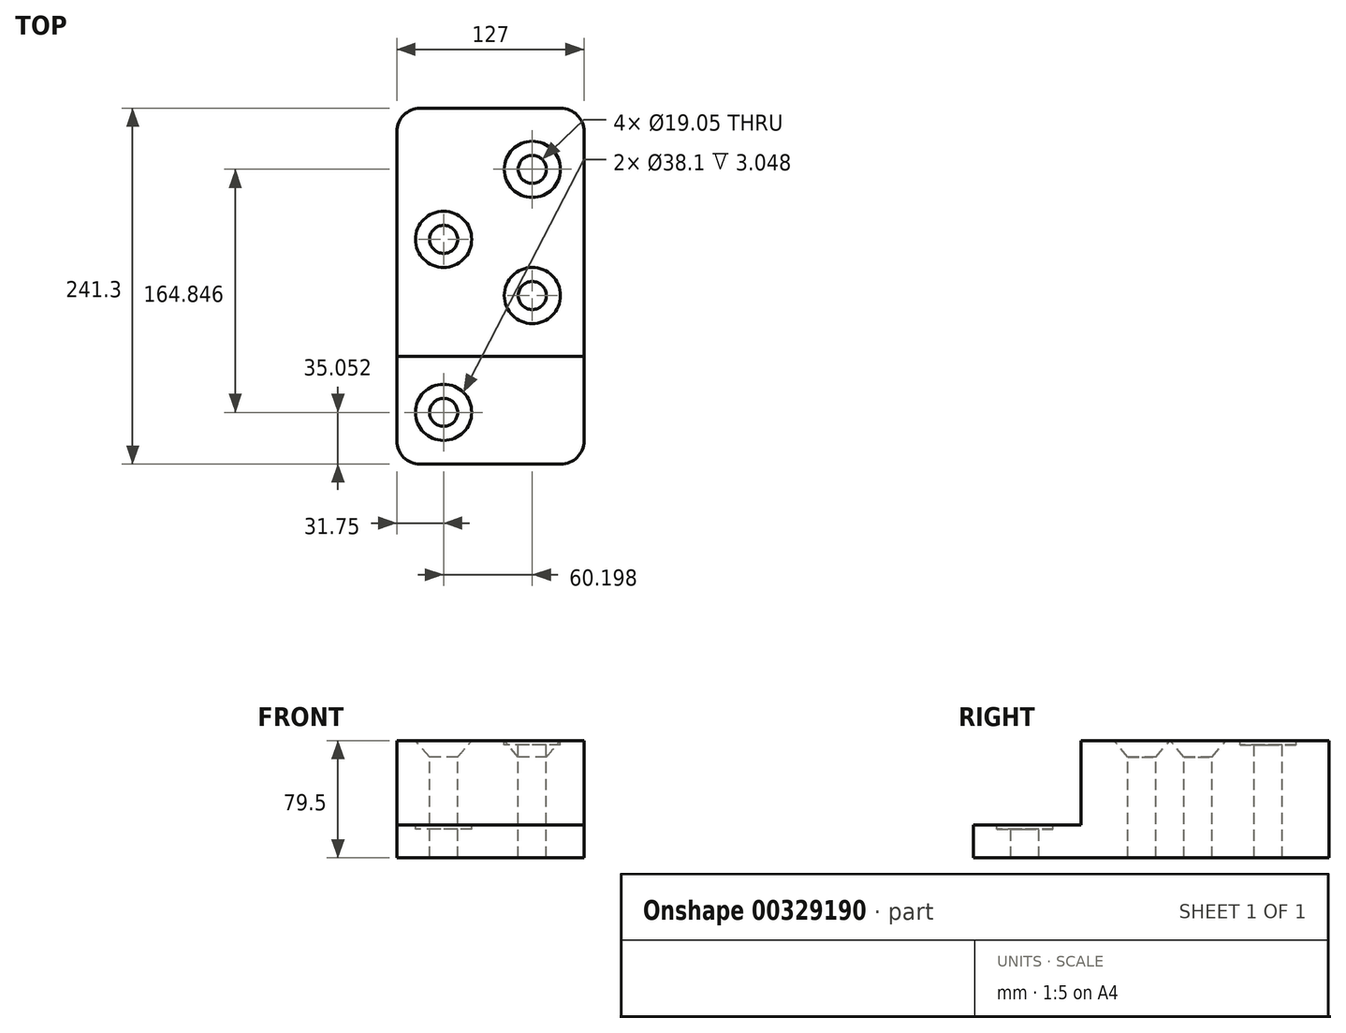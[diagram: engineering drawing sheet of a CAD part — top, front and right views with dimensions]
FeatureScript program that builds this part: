
annotation { "Feature Type Name" : "Feature", "Feature Type Description" : "" }
export const myFeature = defineFeature(function(context is Context, id is Id, definition is map)
    precondition{}
    {
        {
            var Q0;
            Q0=qCreatedBy(makeId("Front.planeOp"),FACE);
            var sketch = newSketch(context, id + "F0", { "sketchPlane" : qUnion([Q0])});
            skLineSegment(sketch, "E0.bottom", {"start": v(0, 0) * mm, "end": v(127, 0) * mm});
            skLineSegment(sketch, "E0.top", {"start": v(0, 79.5) * mm, "end": v(127, 79.5) * mm});
            skLineSegment(sketch, "E0.left", {"start": v(0, 0) * mm, "end": v(0, 79.5) * mm});
            skLineSegment(sketch, "E0.right", {"start": v(127, 0) * mm, "end": v(127, 79.5) * mm});
            skSolve(sketch);
        }
        {
            var Q0;
            Q0 = qSketchRegion(id + "F0", true);
            extrude(context, id + "F1", {"entities" : qUnion([Q0]), "depth" : 241.3 * mm});
        }
        {
            var Q0;
            Q0=makeQuery(id+"F1.opExtrude","SWEPT_FACE",FACE,{"disambiguationData":[OSD([sQuery(id+"F0.wireOp",EDGE,"E0.top")])]});
            var sketch = newSketch(context, id + "F2", { "sketchPlane" : qUnion([Q0])});
            skLineSegment(sketch, "E1.bottom", {"start": v(0, -241.3) * mm, "end": v(127, -241.3) * mm});
            skLineSegment(sketch, "E1.top", {"start": v(0, -168.4) * mm, "end": v(127, -168.4) * mm});
            skLineSegment(sketch, "E1.left", {"start": v(0, -241.3) * mm, "end": v(0, -168.4) * mm});
            skLineSegment(sketch, "E1.right", {"start": v(127, -241.3) * mm, "end": v(127, -168.4) * mm});
            skSolve(sketch);
        }
        {
            var Q0;
            Q0 = qSketchRegion(id + "F2", true);
            extrude(context, id + "F3", {"entities" : qUnion([Q0]), "operationType" : NewBodyOperationType.REMOVE, "oppositeDirection" : true, "depth" : 57.15 * mm});
        }
        {
            var Q0;
            Q0=makeQuery(id+"F1.opExtrude","CAP_EDGE",EDGE,{"disambiguationData":[OSD([sQuery(id+"F0.wireOp",EDGE,"E0.right")])],"isStart":true});
            var Q1;
            Q1=makeQuery(id+"F1.opExtrude","CAP_EDGE",EDGE,{"disambiguationData":[OSD([sQuery(id+"F0.wireOp",EDGE,"E0.left")])],"isStart":true});
            var Q2;
            Q2=makeQuery(id+"F3.boolean.opBoolean","COPY",EDGE,{"derivedFrom":makeQuery(id+"F3.opExtrude","SWEPT_EDGE",EDGE,{"disambiguationData":[OSD([sQuery(id+"F0.wireOp",EDGE,"E0.top"),sQuery(id+"F0.wireOp",EDGE,"E0.left"),sQuery(id+"F2.wireOp",EDGE,"E1.top"),sQuery(id+"F2.wireOp",EDGE,"E1.left")])]})});
            var Q3;
            Q3=makeQuery(id+"F3.boolean.opBoolean","COPY",EDGE,{"derivedFrom":makeQuery(id+"F3.opExtrude","SWEPT_EDGE",EDGE,{"disambiguationData":[OSD([sQuery(id+"F0.wireOp",EDGE,"E0.top"),sQuery(id+"F0.wireOp",EDGE,"E0.right"),sQuery(id+"F2.wireOp",EDGE,"E1.top"),sQuery(id+"F2.wireOp",EDGE,"E1.right")])]})});
            var Q4;
            Q4=makeQuery(id+"F1.opExtrude","CAP_EDGE",EDGE,{"disambiguationData":[OSD([sQuery(id+"F0.wireOp",EDGE,"E0.right")])],"isStart":false});
            var Q5;
            Q5=makeQuery(id+"F1.opExtrude","CAP_EDGE",EDGE,{"disambiguationData":[OSD([sQuery(id+"F0.wireOp",EDGE,"E0.left")])],"isStart":false});
            fillet(context, id + "F4", {"entities" : qUnion([Q0, Q1, Q2, Q3, Q4, Q5]), "radius" : 15.75 * mm, "tangentPropagation" : true, "allowEdgeOverflow" : false});
        }
        {
            var Q0;
            Q0=makeQuery(id+"F1.opExtrude","SWEPT_FACE",FACE,{"disambiguationData":[OSD([sQuery(id+"F0.wireOp",EDGE,"E0.top")])]});
            var sketch = newSketch(context, id + "F5", { "sketchPlane" : qUnion([Q0])});
            skCircle(sketch, "E2", {"center": v(91.95, -41.4) * mm, "radius": 19.05 * mm});
            skSolve(sketch);
        }
        {
            var Q0;
            Q0 = qSketchRegion(id + "F5", true);
            extrude(context, id + "F6", {"entities" : qUnion([Q0]), "operationType" : NewBodyOperationType.REMOVE, "oppositeDirection" : true, "depth" : 3.05 * mm});
        }
        {
            var Q0;
            Q0=makeQuery(id+"F6.boolean.opBoolean","COPY",FACE,{"derivedFrom":makeQuery(id+"F6.opExtrude","CAP_FACE",FACE,{"disambiguationData":[OSD([sQuery(id+"F5.wireOp",EDGE,"E2")])],"isStart":false})});
            var sketch = newSketch(context, id + "F7", { "sketchPlane" : qUnion([Q0])});
            skCircle(sketch, "E3", {"center": v(91.95, -41.4) * mm, "radius": 9.53 * mm});
            skSolve(sketch);
        }
        {
            var Q0;
            Q0 = qSketchRegion(id + "F7", true);
            extrude(context, id + "F8", {"entities" : qUnion([Q0]), "operationType" : NewBodyOperationType.REMOVE, "endBound" : BoundingType.THROUGH_ALL, "oppositeDirection" : true, "depth" : 25.4 * mm});
        }
        {
            var Q0;
            Q0=makeQuery(id+"F1.opExtrude","SWEPT_FACE",FACE,{"disambiguationData":[OSD([sQuery(id+"F0.wireOp",EDGE,"E0.top")])]});
            var sketch = newSketch(context, id + "F9", { "sketchPlane" : qUnion([Q0])});
            skCircle(sketch, "E4", {"center": v(31.75, -88.9) * mm, "radius": 19.05 * mm});
            skCircle(sketch, "E5", {"center": v(91.95, -127) * mm, "radius": 19.05 * mm});
            skSolve(sketch);
        }
        {
            var Q0;
            Q0=sQuery(id+"F9.wireOp",VERTEX,"E4.center");
            var Q1;
            Q1=sQuery(id+"F9.wireOp",VERTEX,"E5.center");
            var Q2;
            Q2=makeQuery(id+"F1.opExtrude","SWEPT_BODY",BODY,{"disambiguationData":[OSD([sQuery(id+"F0.wireOp",EDGE,"E0.bottom"),sQuery(id+"F0.wireOp",EDGE,"E0.top"),sQuery(id+"F0.wireOp",EDGE,"E0.left"),sQuery(id+"F0.wireOp",EDGE,"E0.right")])]});
            hole(context, id + "F10", {"style" : HoleStyle.C_SINK, "endStyle" : HoleEndStyle.THROUGH, "holeDiameter" : 19.05 * mm, "cSinkDiameter" : 38.1 * mm, "cSinkAngle" : 81 * degree, "tappedDepth" : 12.7 * mm, "tapClearance" : 3, "locations" : qUnion([Q0, Q1]), "scope" : qUnion([Q2])});
        }
        {
            var Q0;
            Q0=makeQuery(id+"F3.boolean.opBoolean","COPY",FACE,{"derivedFrom":makeQuery(id+"F3.opExtrude","CAP_FACE",FACE,{"disambiguationData":[OSD([sQuery(id+"F2.wireOp",EDGE,"E1.bottom"),sQuery(id+"F2.wireOp",EDGE,"E1.top"),sQuery(id+"F2.wireOp",EDGE,"E1.left"),sQuery(id+"F2.wireOp",EDGE,"E1.right")])],"isStart":false})});
            var sketch = newSketch(context, id + "F11", { "sketchPlane" : qUnion([Q0])});
            skCircle(sketch, "E6", {"center": v(31.75, -206.25) * mm, "radius": 19.05 * mm});
            skSolve(sketch);
        }
        {
            var Q0;
            Q0 = qSketchRegion(id + "F11", true);
            extrude(context, id + "F12", {"entities" : qUnion([Q0]), "operationType" : NewBodyOperationType.REMOVE, "oppositeDirection" : true, "depth" : 3.05 * mm});
        }
        {
            var Q0;
            Q0=makeQuery(id+"F12.boolean.opBoolean","COPY",FACE,{"derivedFrom":makeQuery(id+"F12.opExtrude","CAP_FACE",FACE,{"disambiguationData":[OSD([sQuery(id+"F11.wireOp",EDGE,"E6")])],"isStart":false})});
            var sketch = newSketch(context, id + "F13", { "sketchPlane" : qUnion([Q0])});
            skCircle(sketch, "E7", {"center": v(31.75, -206.25) * mm, "radius": 9.53 * mm});
            skSolve(sketch);
        }
        {
            var Q0;
            Q0 = qSketchRegion(id + "F13", true);
            extrude(context, id + "F14", {"entities" : qUnion([Q0]), "operationType" : NewBodyOperationType.REMOVE, "endBound" : BoundingType.THROUGH_ALL, "oppositeDirection" : true, "depth" : 25.4 * mm});
        }
    });
